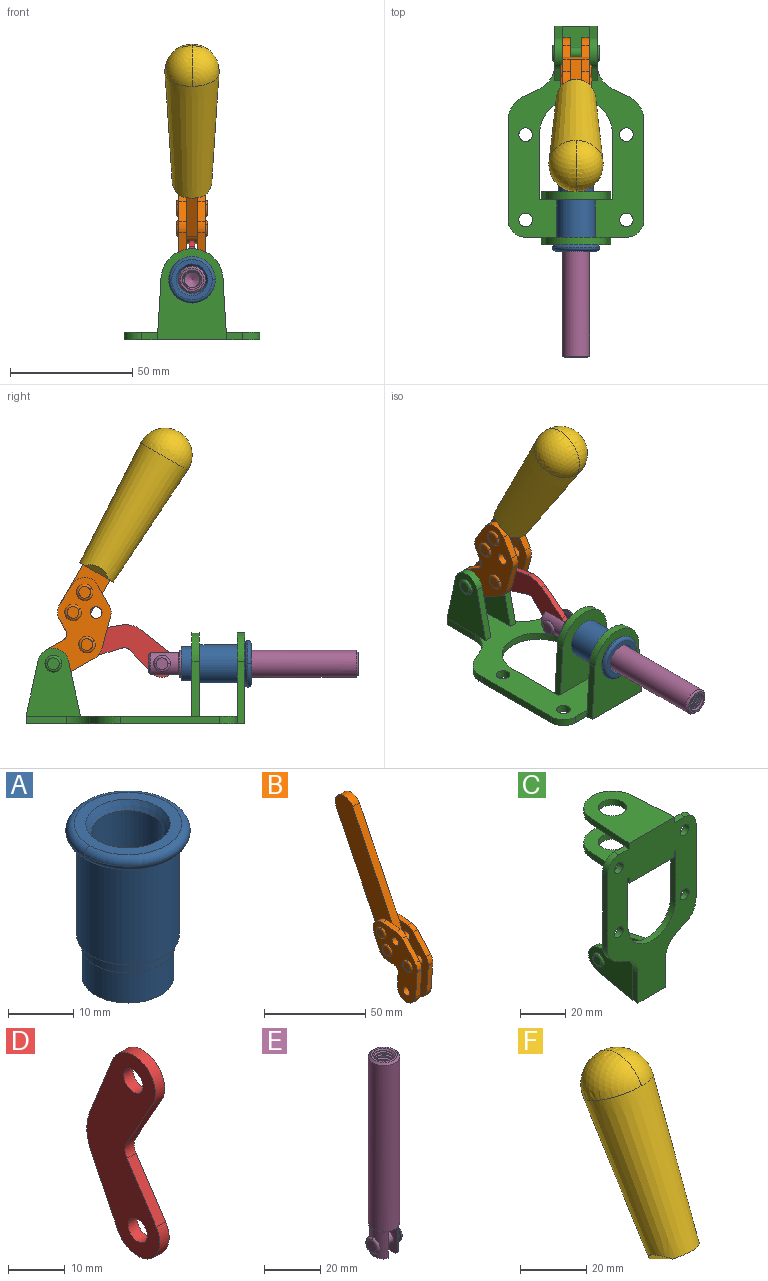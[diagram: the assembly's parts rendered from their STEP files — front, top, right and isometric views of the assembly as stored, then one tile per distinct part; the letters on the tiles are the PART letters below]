
ASSEMBLY  parts=6 mates=6
PART A: 15 faces, bbox 20.6x20.6x28.7 mm
  f0: torus R=8.26mm, axis (0,0,1), area 56.8mm2, adj f1,f10,f12
  f1: torus R=8.26mm, axis (0,0,1), area 56.8mm2, adj f0,f6,f13
  f2: cylinder r=5.59mm len=25.91mm, axis (0,0,1), area 909.6mm2, adj f3,f4
  f3: cone r=6.86mm half-angle=45deg, axis (0,0,-1), area 70.2mm2, adj f2,f14
  f4: cone r=6.47mm half-angle=30deg, axis (0,0,1), area 66.7mm2, adj f2,f13
  f5: cylinder r=7.04mm len=14.07mm, axis (0,0,1), area 252.6mm2, adj f11,f14
  f6: torus R=8.26mm, axis (0,0,1), area 56.8mm2, adj f1,f12,f13
  f7: cylinder r=7.16mm len=14.33mm, axis (0,0,1), area 91.5mm2, adj f9,f11
  f8: cylinder r=7.86mm len=18.42mm, axis (0,0,1), area 909.6mm2, adj f9,f10
  f9: plane 15.72x15.72mm, normal (0,0,-1), area 33mm2, adj f7,f8
  f10: plane 16.51x16.51mm, normal (0,0,-1), area 19.9mm2, adj f0,f8,f12
  f11: plane 14.33x14.33mm, normal (0,0,-1), area 5.7mm2, adj f5,f7
  f12: torus R=8.26mm, axis (0,0,1), area 56.8mm2, adj f0,f6,f10
  f13: plane 16.51x16.51mm, normal (0,0,1), area 82.7mm2, adj f1,f4,f6
  f14: plane 14.07x14.07mm, normal (0,0,-1), area 7.8mm2, adj f3,f5
PART B: 59 faces, bbox 12.9x60.2x99.6 mm
  f0: torus R=2.39mm, axis (-1,0,0), area 14.9mm2, adj f20,f43,f51
  f1: torus R=2.39mm, axis (-1,0,0), area 14.9mm2, adj f19,f42,f51
  f2: torus R=2.39mm, axis (-1,0,0), area 14.9mm2, adj f18,f35,f51
  f3: torus R=2.39mm, axis (-1,0,0), area 14.9mm2, adj f14,f17,f23
  f4: torus R=2.39mm, axis (-1,0,0), area 14.9mm2, adj f13,f16,f23
  f5: torus R=2.39mm, axis (-1,0,0), area 14.9mm2, adj f12,f15,f23
  f6: cylinder r=2.39mm len=4.78mm, axis (1,0,0), area 46.5mm2, adj f48,f50,f51
  f7: cylinder r=2.39mm len=4.78mm, axis (1,0,0), area 46.5mm2, adj f50,f51
  f8: cylinder r=6.35mm len=12.68mm, axis (1,0,0), area 61.8mm2, adj f38,f39,f50,f51
  f9: cylinder r=2.39mm len=4.78mm, axis (-1,0,0), area 70.5mm2, adj f46,f50
  f10: cylinder r=2.39mm len=4.78mm, axis (-1,0,0), area 46.5mm2, adj f23,f45,f46
  f11: cylinder r=2.39mm len=4.78mm, axis (-1,0,0), area 46.5mm2, adj f23,f46
  f12: plane 4.78x4.78mm, normal (1,0,0), area 17.9mm2, adj f5,f15
  f13: plane 4.78x4.78mm, normal (1,0,0), area 17.9mm2, adj f4,f16
  f14: plane 4.78x4.78mm, normal (1,0,0), area 17.9mm2, adj f3,f17
  f15: torus R=2.39mm, axis (-1,0,0), area 14.9mm2, adj f5,f12,f23
  f16: torus R=2.39mm, axis (-1,0,0), area 14.9mm2, adj f4,f13,f23
  f17: torus R=2.39mm, axis (-1,0,0), area 14.9mm2, adj f3,f14,f23
  f18: plane 4.78x4.78mm, normal (-1,0,0), area 17.9mm2, adj f2,f35
  f19: plane 4.78x4.78mm, normal (-1,0,0), area 17.9mm2, adj f1,f42
  f20: plane 4.78x4.78mm, normal (-1,0,0), area 17.9mm2, adj f0,f43
  f21: plane 2.26x0.2mm, normal (1,0,0), area 0.2mm2, adj f31,f44
  f22: plane 2.26x0.2mm, normal (-1,0,0), area 0.2mm2, adj f41,f44
  f23: plane 39.37x30.77mm, normal (1,0,0), area 565.5mm2, adj f3,f4,f5,f10,f11,f15,f16,f17
  f24: cylinder r=6.1mm len=4.15mm, axis (-1,0,0), area 14.7mm2, adj f23,f25,f32,f46
  f25: plane 10.25x9.01mm, normal (0,-0.75,0.66), area 42.3mm2, adj f23,f24,f26,f46
  f26: cylinder r=6.35mm len=4.64mm, axis (-1,0,0), area 15.6mm2, adj f23,f25,f27,f46
  f27: plane 15.84x3.1mm, normal (0,-1,-0.07), area 49.2mm2, adj f23,f26,f28,f46
  f28: cylinder r=6.35mm len=12.68mm, axis (-1,0,0), area 61.8mm2, adj f23,f27,f29,f46
  f29: plane 8.11x3.1mm, normal (0,1,0.07), area 25.2mm2, adj f23,f28,f30,f46
  f30: cylinder r=3.05mm len=3.25mm, axis (-1,0,0), area 14.8mm2, adj f23,f29,f31,f46
  f31: plane 5.99x3.1mm, normal (0,0.07,-1), area 18.6mm2, adj f21,f23,f30,f44,f46
  f32: plane 9.5x3.1mm, normal (0,-0.07,1), area 29.5mm2, adj f23,f24,f33,f46,f47
  f33: cylinder r=6.1mm len=8.63mm, axis (-1,0,0), area 39.1mm2, adj f23,f32,f34,f47
  f34: plane 8.65x3.96mm, normal (0,0.91,-0.42), area 29.5mm2, adj f23,f33,f44,f47
  f35: torus R=2.39mm, axis (-1,0,0), area 14.9mm2, adj f2,f18,f51
  f36: plane 10.25x9.01mm, normal (0,-0.75,0.66), area 42.3mm2, adj f37,f49,f50,f51
  f37: cylinder r=6.35mm len=4.64mm, axis (1,0,0), area 15.6mm2, adj f36,f38,f50,f51
  f38: plane 15.84x3.1mm, normal (0,-1,-0.07), area 49.2mm2, adj f8,f37,f50,f51
  f39: plane 8.11x3.1mm, normal (0,1,0.07), area 25.2mm2, adj f8,f40,f50,f51
  f40: cylinder r=3.05mm len=3.25mm, axis (1,0,0), area 14.8mm2, adj f39,f41,f50,f51
  f41: plane 5.99x3.1mm, normal (0,0.07,-1), area 18.6mm2, adj f22,f40,f44,f50,f51
  f42: torus R=2.39mm, axis (-1,0,0), area 14.9mm2, adj f1,f19,f51
  f43: torus R=2.39mm, axis (-1,0,0), area 14.9mm2, adj f0,f20,f51
  f44: cylinder r=6.35mm len=12.12mm, axis (-1,0,0), area 128.9mm2, adj f21,f22,f23,f31,f34,f41,f46,f47
  f45: plane 2.65x1.35mm, normal (1,0,0), area 1mm2, adj f10,f55
  f46: plane 39.08x20.42mm, normal (-1,0,0), area 412.5mm2, adj f9,f10,f11,f24,f25,f26,f27,f28
  f47: plane 77.62x39.82mm, normal (1,0,0), area 850mm2, adj f32,f33,f34,f44,f53,f54,f55
  f48: plane 2.65x1.35mm, normal (-1,0,0), area 1mm2, adj f6,f55
  f49: cylinder r=6.1mm len=4.15mm, axis (1,0,0), area 14.7mm2, adj f36,f50,f51,f56
  f50: plane 39.08x20.42mm, normal (1,0,0), area 412.5mm2, adj f6,f7,f8,f9,f36,f37,f38,f39
  f51: plane 39.37x30.77mm, normal (-1,0,0), area 565.5mm2, adj f0,f1,f2,f6,f7,f8,f35,f36
  f52: plane 8.65x3.96mm, normal (0,0.91,-0.42), area 29.5mm2, adj f44,f51,f57,f58
  f53: plane 68.49x33.4mm, normal (0,0.9,-0.44), area 358.1mm2, adj f44,f47,f54,f58
  f54: cylinder r=6.35mm len=12.06mm, axis (1,0,0), area 93.7mm2, adj f47,f53,f55,f58
  f55: plane 68.49x33.4mm, normal (0,-0.9,0.44), area 358.1mm2, adj f44,f45,f46,f47,f48,f50,f54,f58
  f56: plane 9.5x3.1mm, normal (0,-0.07,1), area 29.5mm2, adj f49,f50,f51,f57,f58
  f57: cylinder r=6.1mm len=8.63mm, axis (1,0,0), area 39.1mm2, adj f51,f52,f56,f58
  f58: plane 77.62x39.82mm, normal (-1,0,0), area 850mm2, adj f44,f52,f53,f54,f55,f56,f57
PART C: 55 faces, bbox 55.7x37.4x89.8 mm
  f0: torus R=2.41mm, axis (-1,0,0), area 15mm2, adj f11,f15,f25
  f1: torus R=2.41mm, axis (-1,0,0), area 15mm2, adj f10,f12,f22
  f2: cylinder r=2.78mm len=5.56mm, axis (0,-1,0), area 54.2mm2, adj f30,f54
  f3: cylinder r=14.99mm len=29.97mm, axis (0,-1,0), area 145.9mm2, adj f30,f49,f53,f54
  f4: cylinder r=2.78mm len=5.56mm, axis (0,-1,0), area 54.2mm2, adj f30,f54
  f5: cylinder r=2.78mm len=5.56mm, axis (0,-1,0), area 54.2mm2, adj f30,f54
  f6: cylinder r=2.78mm len=5.56mm, axis (0,-1,0), area 54.2mm2, adj f30,f54
  f7: cylinder r=6.35mm len=12.7mm, axis (0,0,1), area 123.6mm2, adj f27,f51
  f8: cylinder r=6.35mm len=12.7mm, axis (0,0,-1), area 124.7mm2, adj f21,f35
  f9: cylinder r=2.41mm len=11.18mm, axis (-1,0,0), area 169.4mm2, adj f16,f19
  f10: plane 4.83x4.83mm, normal (1,0,0), area 18.3mm2, adj f1,f12
  f11: plane 4.83x4.83mm, normal (-1,0,0), area 18.3mm2, adj f0,f15
  f12: torus R=2.41mm, axis (-1,0,0), area 15mm2, adj f1,f10,f22
  f13: cylinder r=6.35mm len=12.41mm, axis (1,0,0), area 53.4mm2, adj f18,f19,f22,f23
  f14: cylinder r=6.35mm len=12.41mm, axis (-1,0,0), area 53.4mm2, adj f16,f17,f24,f25
  f15: torus R=2.41mm, axis (-1,0,0), area 15mm2, adj f0,f11,f25
  f16: plane 27.86x22.35mm, normal (1,0,0), area 425.4mm2, adj f9,f14,f17,f24,f30
  f17: plane 22.86x4.97mm, normal (0,0.21,0.98), area 72.5mm2, adj f14,f16,f25,f30
  f18: plane 22.86x4.97mm, normal (0,0.21,0.98), area 72.5mm2, adj f13,f19,f22,f30
  f19: plane 27.86x22.35mm, normal (-1,0,0), area 425.4mm2, adj f9,f13,f18,f23,f30
  f20: cylinder r=12.7mm len=25.35mm, axis (0,0,-1), area 119.8mm2, adj f21,f34,f35,f36
  f21: plane 34.21x28.07mm, normal (0,0,-1), area 702.4mm2, adj f8,f20,f30,f34,f36
  f22: plane 27.96x22.45mm, normal (1,0,0), area 407.2mm2, adj f1,f12,f13,f18,f23,f30,f42,f43
  f23: plane 22.86x4.97mm, normal (0,0.21,-0.98), area 72.5mm2, adj f13,f19,f22,f44
  f24: plane 22.86x4.97mm, normal (0,0.21,-0.98), area 72.5mm2, adj f14,f16,f25,f44
  f25: plane 27.86x22.35mm, normal (-1,0,0), area 407.1mm2, adj f0,f14,f15,f17,f24,f30,f45,f46
  f26: plane 3.1x0.95mm, normal (0,0,-1), area 2.7mm2, adj f30,f49,f50,f54
  f27: plane 34.21x28.07mm, normal (0,0,1), area 702.4mm2, adj f7,f28,f30,f50,f52
  f28: cylinder r=12.7mm len=25.35mm, axis (0,0,1), area 118.8mm2, adj f27,f50,f51,f52
  f29: plane 3.1x0.95mm, normal (0,0,-1), area 2.7mm2, adj f30,f52,f53,f54
  f30: plane 86.54x55.63mm, normal (0,1,0), area 2362.9mm2, adj f2,f3,f4,f5,f6,f16,f17,f18
  f31: plane 40.56x3.1mm, normal (-1,0,0), area 125.7mm2, adj f30,f32,f48,f54
  f32: cylinder r=7.11mm len=7.11mm, axis (0,-1,0), area 34.6mm2, adj f30,f31,f33,f54
  f33: plane 6.67x3.1mm, normal (0,0,1), area 20.4mm2, adj f30,f32,f34,f54
  f34: plane 25.39x3.13mm, normal (-1,0.06,0), area 79.5mm2, adj f20,f21,f33,f35,f54
  f35: plane 37.31x28.45mm, normal (0,0,1), area 789.9mm2, adj f8,f20,f34,f36,f54
  f36: plane 25.39x3.13mm, normal (1,0.06,0), area 79.5mm2, adj f20,f21,f35,f37,f54
  f37: plane 6.67x3.1mm, normal (0,0,1), area 20.4mm2, adj f30,f36,f38,f54
  f38: cylinder r=7.11mm len=7.11mm, axis (0,-1,0), area 34.6mm2, adj f30,f37,f39,f54
  f39: plane 40.56x3.1mm, normal (1,0,0), area 125.7mm2, adj f30,f38,f40,f54
  f40: cylinder r=11.18mm len=10.16mm, axis (0,-1,0), area 39.5mm2, adj f30,f39,f41,f54
  f41: plane 6.09x3.1mm, normal (0.42,0,-0.91), area 20.8mm2, adj f30,f40,f42,f54
  f42: cylinder r=11.18mm len=9.41mm, axis (0,-1,0), area 37.2mm2, adj f22,f30,f41,f43,f54
  f43: plane 16.5x3.1mm, normal (1,0,0), area 51.1mm2, adj f22,f42,f44,f54
  f44: plane 17.37x3.1mm, normal (0,0,-1), area 53.8mm2, adj f23,f24,f30,f43,f45,f54
  f45: plane 16.5x3.1mm, normal (-1,0,0), area 51.1mm2, adj f25,f44,f46,f54
  f46: cylinder r=11.18mm len=9.41mm, axis (0,-1,0), area 37.2mm2, adj f25,f30,f45,f47,f54
  f47: plane 6.09x3.1mm, normal (-0.42,0,-0.91), area 20.8mm2, adj f30,f46,f48,f54
  f48: cylinder r=11.18mm len=10.16mm, axis (0,-1,0), area 39.5mm2, adj f30,f31,f47,f54
  f49: plane 26.54x3.1mm, normal (-1,0,0), area 82.3mm2, adj f3,f26,f30,f54
  f50: plane 25.39x3.1mm, normal (1,0.06,0), area 78.8mm2, adj f26,f27,f28,f51,f54
  f51: plane 37.31x28.45mm, normal (0,0,-1), area 789.9mm2, adj f7,f28,f50,f52,f54
  f52: plane 25.39x3.1mm, normal (-1,0.06,0), area 78.8mm2, adj f27,f28,f29,f51,f54
  f53: plane 26.54x3.1mm, normal (1,0,0), area 82.3mm2, adj f3,f29,f30,f54
  f54: plane 89.66x55.63mm, normal (0,-1,0), area 2678.5mm2, adj f2,f3,f4,f5,f6,f26,f29,f31
PART D: 12 faces, bbox 2.3x18.2x42.8 mm
  f0: cylinder r=2.4mm len=4.8mm, axis (1,0,0), area 34.9mm2, adj f4,f11
  f1: cylinder r=10.41mm len=8.47mm, axis (1,0,0), area 20.2mm2, adj f4,f9,f10,f11
  f2: cylinder r=3.05mm len=3.16mm, axis (1,0,0), area 7.7mm2, adj f4,f6,f7,f11
  f3: cylinder r=2.4mm len=4.8mm, axis (1,0,0), area 34.9mm2, adj f4,f11
  f4: plane 42.81x18.23mm, normal (-1,0,0), area 414.1mm2, adj f0,f1,f2,f3,f5,f6,f7,f8
  f5: cylinder r=5.54mm len=10.67mm, axis (1,0,0), area 41.8mm2, adj f4,f6,f10,f11
  f6: plane 11.66x6.53mm, normal (0,-0.87,-0.49), area 30.9mm2, adj f2,f4,f5,f11
  f7: plane 11.17x7.33mm, normal (0,-0.84,0.55), area 30.9mm2, adj f2,f4,f8,f11
  f8: cylinder r=5.54mm len=10.51mm, axis (1,0,0), area 41.8mm2, adj f4,f7,f9,f11
  f9: plane 13.67x6.67mm, normal (0,0.9,-0.44), area 35.1mm2, adj f1,f4,f8,f11
  f10: plane 14.1x5.7mm, normal (0,0.93,0.37), area 35.1mm2, adj f1,f4,f5,f11
  f11: plane 42.81x18.23mm, normal (1,0,0), area 414.1mm2, adj f0,f1,f2,f3,f5,f6,f7,f8
PART E: 48 faces, bbox 12.6x11.1x86.1 mm
  f0: torus R=2.41mm, axis (-1,0,0), area 15mm2, adj f30,f32,f34
  f1: torus R=2.41mm, axis (-1,0,0), area 15mm2, adj f29,f31,f33
  f2: cylinder r=5.54mm len=72.39mm, axis (0,0,1), area 2518.5mm2, adj f3,f4,f42,f43
  f3: cone r=5.54mm half-angle=45deg, axis (0,0,1), area 7.6mm2, adj f2,f5,f41
  f4: cone r=5.54mm half-angle=45deg, axis (0,0,-1), area 34.9mm2, adj f2,f39
  f5: cylinder r=5.08mm len=11.48mm, axis (0,0,1), area 108.3mm2, adj f3,f7,f8,f41
  f6: cylinder r=2.41mm len=4.83mm, axis (-1,0,0), area 71.2mm2, adj f40,f41
  f7: cylinder r=2.41mm len=4.83mm, axis (-1,0,0), area 7.6mm2, adj f5,f34
  f8: cone r=5.08mm half-angle=45deg, axis (0,0,1), area 10.6mm2, adj f5,f37,f41
  f9: cone r=3.98mm half-angle=45deg, axis (0,0,1), area 17.6mm2, adj f27,f39,f45,f46,f47
  f10: cylinder r=2.41mm len=4.83mm, axis (-1,0,0), area 7.6mm2, adj f33,f38
  f11: cylinder r=3.2mm len=6.4mm, axis (0,0,1), area 78.4mm2, adj f12,f28,f44,f45,f47
  f12: cylinder r=3.2mm len=6.4mm, axis (0,0,1), area 10.5mm2, adj f11,f13,f45,f47
  f13: cylinder r=3.2mm len=6.4mm, axis (0,0,1), area 10.5mm2, adj f12,f14,f45,f47
  f14: cylinder r=3.2mm len=6.4mm, axis (0,0,1), area 10.5mm2, adj f13,f15,f45,f47
  f15: cylinder r=3.2mm len=6.4mm, axis (0,0,1), area 10.5mm2, adj f14,f16,f45,f47
  f16: cylinder r=3.2mm len=6.4mm, axis (0,0,1), area 10.5mm2, adj f15,f17,f45,f47
  f17: cylinder r=3.2mm len=6.4mm, axis (0,0,1), area 10.5mm2, adj f16,f18,f45,f47
  f18: cylinder r=3.2mm len=6.4mm, axis (0,0,1), area 10.5mm2, adj f17,f19,f45,f47
  f19: cylinder r=3.2mm len=6.4mm, axis (0,0,1), area 10.5mm2, adj f18,f20,f45,f47
  f20: cylinder r=3.2mm len=6.4mm, axis (0,0,1), area 10.5mm2, adj f19,f21,f45,f47
  f21: cylinder r=3.2mm len=6.4mm, axis (0,0,1), area 10.5mm2, adj f20,f22,f45,f47
  f22: cylinder r=3.2mm len=6.4mm, axis (0,0,1), area 10.5mm2, adj f21,f23,f45,f47
  f23: cylinder r=3.2mm len=6.4mm, axis (0,0,1), area 10.5mm2, adj f22,f24,f45,f47
  f24: cylinder r=3.2mm len=6.4mm, axis (0,0,1), area 10.5mm2, adj f23,f25,f45,f47
  f25: cylinder r=3.2mm len=6.4mm, axis (0,0,1), area 10.5mm2, adj f24,f26,f45,f47
  f26: cylinder r=3.2mm len=6.4mm, axis (0,0,1), area 10.5mm2, adj f25,f27,f45,f47
  f27: cylinder r=3.2mm len=6.4mm, axis (0,0,1), area 7.4mm2, adj f9,f26,f45,f47
  f28: cone r=3.2mm half-angle=60deg, axis (0,0,1), area 37.2mm2, adj f11
  f29: plane 4.83x4.83mm, normal (-1,0,0), area 18.3mm2, adj f1,f31
  f30: plane 4.83x4.83mm, normal (1,0,0), area 18.3mm2, adj f0,f32
  f31: torus R=2.41mm, axis (-1,0,0), area 15mm2, adj f1,f29,f33
  f32: torus R=2.41mm, axis (-1,0,0), area 15mm2, adj f0,f30,f34
  f33: plane 6.83x6.83mm, normal (1,0,0), area 18.3mm2, adj f1,f10,f31
  f34: plane 6.83x6.83mm, normal (-1,0,0), area 18.3mm2, adj f0,f7,f32
  f35: cone r=5.08mm half-angle=45deg, axis (0,0,1), area 10.6mm2, adj f36,f38,f40
  f36: plane 7.25x1.97mm, normal (0,0,-1), area 10mm2, adj f35,f40
  f37: plane 7.25x1.97mm, normal (0,0,-1), area 10mm2, adj f8,f41
  f38: cylinder r=5.08mm len=11.48mm, axis (0,0,1), area 108.3mm2, adj f10,f35,f40,f42
  f39: plane 9.55x9.55mm, normal (0,0,1), area 22mm2, adj f4,f9
  f40: plane 12.76x10.09mm, normal (1,0,0), area 95.7mm2, adj f6,f35,f36,f38,f42,f43
  f41: plane 12.76x10.09mm, normal (-1,0,0), area 95.7mm2, adj f3,f5,f6,f8,f37,f43
  f42: cone r=5.54mm half-angle=45deg, axis (0,0,1), area 7.6mm2, adj f2,f38,f40
  f43: plane 11.07x4.7mm, normal (0,0,-1), area 50.4mm2, adj f2,f40,f41
  f44: plane 0.89x0.62mm, normal (-1,0,0), area 0.3mm2, adj f11,f45,f46,f47
  f45: bspline ~24.8x7.63mm, area 266.6mm2, adj f9,f11,f12,f13,f14,f15,f16,f17
  f46: bspline ~24.87x7.63mm, area 73.6mm2, adj f9,f44,f45,f47
  f47: bspline ~24.98x7.63mm, area 272.5mm2, adj f9,f11,f12,f13,f14,f15,f16,f17
PART F: 11 faces, bbox 22.3x42.6x64.5 mm
  f0: sphere r=11.13mm, area 411.4mm2, adj f1,f8
  f1: cone r=11.11mm half-angle=3.3deg, axis (0,0.44,0.9), area 3251.8mm2, adj f0,f7,f8,f9,f10
  f2: cylinder r=6.16mm len=11.7mm, axis (1,0,0), area 89.5mm2, adj f3,f4,f5,f6
  f3: plane 60.23x36.75mm, normal (-1,0,0), area 763.6mm2, adj f2,f4,f6,f10
  f4: plane 51.37x25.05mm, normal (0,0.9,-0.44), area 264.2mm2, adj f2,f3,f5,f10
  f5: plane 60.23x36.75mm, normal (1,0,0), area 763.6mm2, adj f2,f4,f6,f10
  f6: plane 51.37x25.05mm, normal (0,-0.9,0.44), area 264.2mm2, adj f2,f3,f5,f10
  f7: plane 9.95x5.95mm, normal (0.71,-0.31,-0.64), area 25.8mm2, adj f1,f10
  f8: sphere r=11.13mm, area 411.4mm2, adj f0,f1
  f9: plane 9.95x5.95mm, normal (-0.71,-0.31,-0.64), area 25.8mm2, adj f1,f10
  f10: plane 14.27x11.38mm, normal (0,-0.44,-0.9), area 106.7mm2, adj f1,f3,f4,f5,f6,f7,f9
PLACE A rot(axis=(1,0,0),90deg) t=(0,9.43,0)mm
PLACE B rot(axis=(1,0,0),56.3deg) t=(0,1.17,21.92)mm
PLACE C rot(axis=(1,0,0),90deg) t=(0,9.43,0)mm fixed
PLACE D rot(axis=(0,-0.63,-0.78),180deg) t=(0,17.87,5.12)mm
PLACE E rot(axis=(1,0,0),90deg) t=(0,12.44,0)mm
PLACE F rot(axis=(1,0,0),56.3deg) t=(0,1.17,21.92)mm
MATE slider E.f2 <-> C.f7  axis (0,-1,0) through (0,-46.34,24.61)mm
MATE revolute D.f3 <-> E.f6  axis (-1,0,0) through (0,-3.03,24.61)mm
MATE revolute C.f0 <-> B.f7  axis (-1,0,0) through (0,41.52,24.61)mm
MATE fastened F.f2 <-> B.f54  axis (1,0,0) through (0,-5.04,111.41)mm
MATE fastened A.f2 <-> C.f7  axis (0,-1,0) through (0,-36.96,24.61)mm
MATE revolute D.f5 <-> B.f4  axis (-1,0,0) through (0,27.73,32.47)mm
